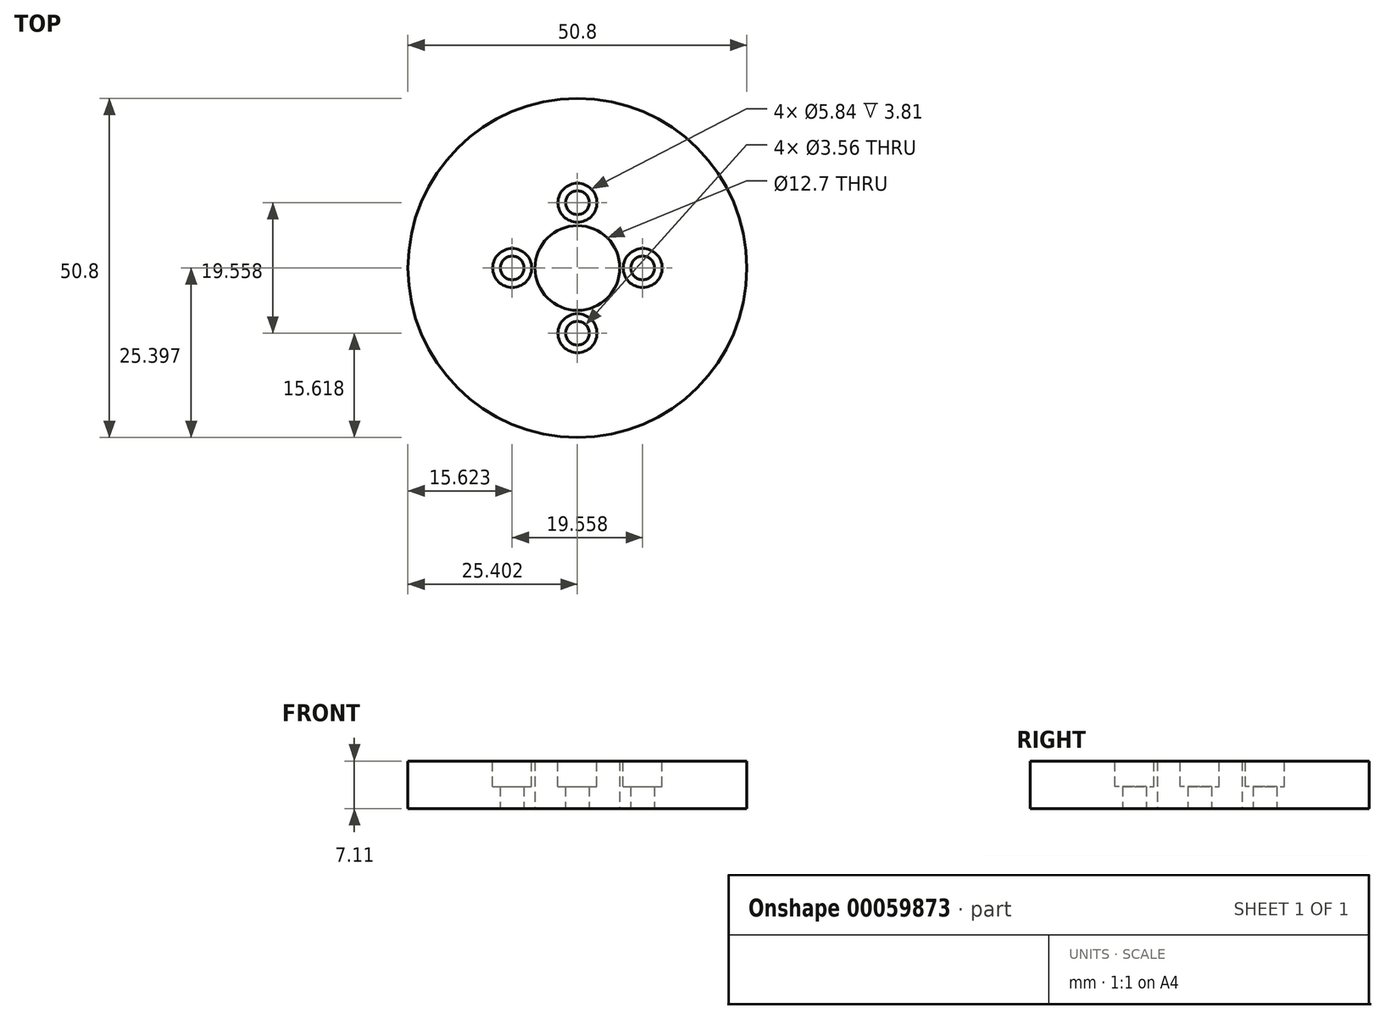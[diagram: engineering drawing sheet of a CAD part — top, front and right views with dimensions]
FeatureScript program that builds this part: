
annotation { "Feature Type Name" : "Feature", "Feature Type Description" : "" }
export const myFeature = defineFeature(function(context is Context, id is Id, definition is map)
    precondition{}
    {
        {
            var Q0;
            Q0=qCreatedBy(makeId("Top.planeOp"),FACE);
            var sketch = newSketch(context, id + "F0", { "sketchPlane" : qUnion([Q0])});
            skCircle(sketch, "E0", {"center": v(-1.89, 2.78) * mm, "radius": 25.4 * mm});
            skCircle(sketch, "E1", {"center": v(-1.89, 2.78) * mm, "radius": 6.35 * mm});
            skSolve(sketch);
        }
        {
            var Q0;
            Q0=qSketchRegion(id+"F0",true);
            extrude(context, id + "F1", {"entities" : qUnion([Q0]), "depth" : 7.11 * mm});
        }
        {
            var Q0;
            Q0=makeQuery(id+"F1.opExtrude","CAP_FACE",FACE,{"disambiguationData":[OSD([sQuery(id+"F0.wireOp",EDGE,"E0"),sQuery(id+"F0.wireOp",EDGE,"E1")])],"isStart":false});
            var sketch = newSketch(context, id + "F2", { "sketchPlane" : qUnion([Q0])});
            skLineSegment(sketch, "E2", {"start": v(-1.89, 2.78) * mm, "end": v(-1.89, 12.56) * mm});
            skLineSegment(sketch, "E3", {"start": v(-1.89, 2.78) * mm, "end": v(-1.89, -7) * mm});
            skLineSegment(sketch, "E4", {"start": v(-1.89, 2.78) * mm, "end": v(-11.67, 2.78) * mm});
            skLineSegment(sketch, "E5", {"start": v(-1.89, 2.78) * mm, "end": v(7.9, 2.78) * mm});
            skCircle(sketch, "E6", {"center": v(-1.89, 12.56) * mm, "radius": 2.92 * mm});
            skCircle(sketch, "E7", {"center": v(-11.67, 2.78) * mm, "radius": 2.92 * mm});
            skCircle(sketch, "E8", {"center": v(7.9, 2.78) * mm, "radius": 2.92 * mm});
            skCircle(sketch, "E9", {"center": v(-1.89, -7) * mm, "radius": 2.92 * mm});
            skSolve(sketch);
        }
        {
            var Q0;
            Q0=qSketchRegion(id+"F2",true);
            extrude(context, id + "F3", {"entities" : qUnion([Q0]), "operationType" : NewBodyOperationType.REMOVE, "oppositeDirection" : true, "depth" : 25.4 * mm});
        }
        {
            var Q0;
            Q0=makeQuery(id+"F1.opExtrude","CAP_FACE",FACE,{"disambiguationData":[OSD([sQuery(id+"F0.wireOp",EDGE,"E0"),sQuery(id+"F0.wireOp",EDGE,"E1")])],"isStart":true});
            var sketch = newSketch(context, id + "F4", { "sketchPlane" : qUnion([Q0])});
            skCircle(sketch, "E10", {"center": v(-1.89, 7) * mm, "radius": 1.78 * mm});
            skCircle(sketch, "E11", {"center": v(7.9, -2.78) * mm, "radius": 1.78 * mm});
            skCircle(sketch, "E12", {"center": v(-1.89, -12.56) * mm, "radius": 1.78 * mm});
            skCircle(sketch, "E13", {"center": v(-11.67, -2.78) * mm, "radius": 1.78 * mm});
            skCircle(sketch, "E14", {"center": v(-1.89, 7) * mm, "radius": 3.18 * mm});
            skCircle(sketch, "E15", {"center": v(7.9, -2.78) * mm, "radius": 3.15 * mm});
            skCircle(sketch, "E16", {"center": v(-1.89, -12.56) * mm, "radius": 3.16 * mm});
            skCircle(sketch, "E17", {"center": v(-11.67, -2.78) * mm, "radius": 3.1 * mm});
            skSolve(sketch);
        }
        {
            var Q0;
            Q0=qSketchRegion(id+"F4",true);
            extrude(context, id + "F5", {"entities" : qUnion([Q0]), "operationType" : NewBodyOperationType.ADD, "oppositeDirection" : true, "depth" : 3.3 * mm});
        }
    });
